# Revit family: Hager-Univers-IP65-D300-H850-Cl.II-encl-NoHosted-AT-de
name_source: partatom
category: Equipement électrique
units: mm (PartAtom-declared; Revit-internal decimal feet)

## family parameters
Basée sur le plan de construction = Oui
Configuration du panneau = Deux colonnes, circuits au sein
Cote de connecteur circulaire = Utiliser le diamètre
Couper avec des vides une fois chargée = Non
Partagée = Non
Point de calcul de pièce = Non
Toujours verticalement = Oui
Type d'élément = Tableau de raccordement

## types (6) — shared parameters
Commentaires du type = Univers
EF000003 - Montageart = EV000384 - Aufputz
EF000007 - Farbe = EV000270 - grau
EF000040 - Höhe = 850 mm  [stored 2.78871 ft]
EF000049 - Tiefe = 300 mm  [stored 0.984252 ft]
EF000116 - RAL-Nummer = 7035
EF000118 - Mit Montageplatte = Non
EF000266 - Anzahl der Reihen = 5
EF001088 - Anbaumöglichkeit = Non
EF001596 - Werkstoff des Gehäuses = EV000139 - Kunststoff
EF001613 - Funktionserhalt = EV000494 - ohne
EF003532 - Geeignet für Außengebrauch = Oui
EF004293 - Schlagfestigkeit = EV008784 - IK10
EF004464 - Art der Tür = EV002646 - Einzel
EF005474 - Schutzart (IP) = EV006421 - IP65
EF006244 - Transparenter Deckel/Tür = Non
EF006306 - Mit Schloss = Oui
EF007800 - Geeignet für Blitzschutz = Oui
EF009170 - Materialstärke Gehäuse = 2 mm  [stored 0.00656168 ft]
EF009171 - Materialstärke Tür/Deckel = 2 mm  [stored 0.00656168 ft]
EF009212 - Ausführung Deckel = EV000116 - geschlossen
EF015940 - Deckel mit Überdruckentlastung = Non
Elévation par défaut = 1219 mm
Fabricant = Hager
HG000002 - Mit tür = Oui
HG000003 - Bereich = Univers
HG000006 - Unterputz = Non
HG000009 - Doppelflügeligen Tür = Non
HG000010 - Asymmetrische Türen = Non
HG000023 - Gehäuse mit doppeltem Querschnitt = Non
HG000024 - Höhe des unteren Teils = 600 mm
HG000026 - Stehend auf dem Boden = Non
zero-valued in all types: EF000218 - Einbautiefe, EF000437 - Anzahl der Leitungseinführungen, EF009554 - Anzahl der Öffnungen für Flanschplatten, HG000027 - Sockelhöhe

## per-type parameters (varying)
| type | EF000008 - Breite | EF000339 - Art der Abdeckung | EF001131 - Innentiefe | EF002950 - Breite in Teilungseinheiten | EF004427 - Anzahl der Module | EF008873 - Nennstrom (In) | HG000004 - Herstellerreferenz |
| Aufputz IP65 B1100 H850 T300  - FL54S | 1100 mm | EV004216 - Tür | 150 mm  [stored 0.492126 ft] | 48 | 240 | 630 A | FL54S |
| Aufputz IP65 B1100 H850 T300  - FL54SP | 1100 mm | EV004216 - Tür | 150 mm  [stored 0.492126 ft] | 48 | 240 | 630 A | FL54SP |
| Aufputz IP65 B600 H850 T300  - FL52S | 600 mm | EV004216 - Tür | 235 mm  [stored 0.770997 ft] | 24 | 120 | 630 A | FL52S |
| Aufputz IP65 B600 H850 T300  - FL52SP | 600 mm | EV004216 - Tür | 235 mm  [stored 0.770997 ft] | 24 | 120 | 400 A | FL52SP |
| Aufputz IP65 B850 H850 T300  - FL53S | 850 mm  [stored 2.78871 ft] | EV001012 - Deckel | 150 mm  [stored 0.492126 ft] | 36 | 180 | 400 A | FL53S |
| Aufputz IP65 B850 H850 T300  - FL53SP | 850 mm  [stored 2.78871 ft] | EV001012 - Deckel | 150 mm  [stored 0.492126 ft] | 36 | 180 | 400 A | FL53SP |

note: [stored X ft] marks values corroborated as IEEE doubles in the binary element streams (Revit-internal decimal feet)

## geometry (parser evidence)
native form markers: Blend x4, Sweep x6
no freeform markers — native parametric forms only
